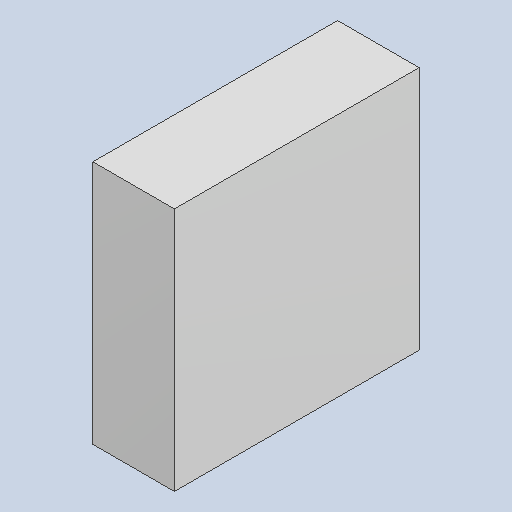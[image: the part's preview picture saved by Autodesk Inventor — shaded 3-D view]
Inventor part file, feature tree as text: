
AUTODESK INVENTOR PART (.ipt)
format: ipt  version: 2023.4 (Build 274418000, 418)  size: 81,408 bytes
history: native  units: mm
features: extrude x1
ambient origin geometry x8: Origin, YZ Plane, XZ Plane, XY Plane, X Axis, Y Axis, Z Axis, Center Point
bodies: Solid1 (feature_tree)
feature tree (1):
  extrude  "Extruded_24"  [1 undecoded]
note: 1 required parameter value undecoded (feature->parameter linkage not recoverable at this tier; creation-order binding heuristic only, values carry confidence <= 0.55)
